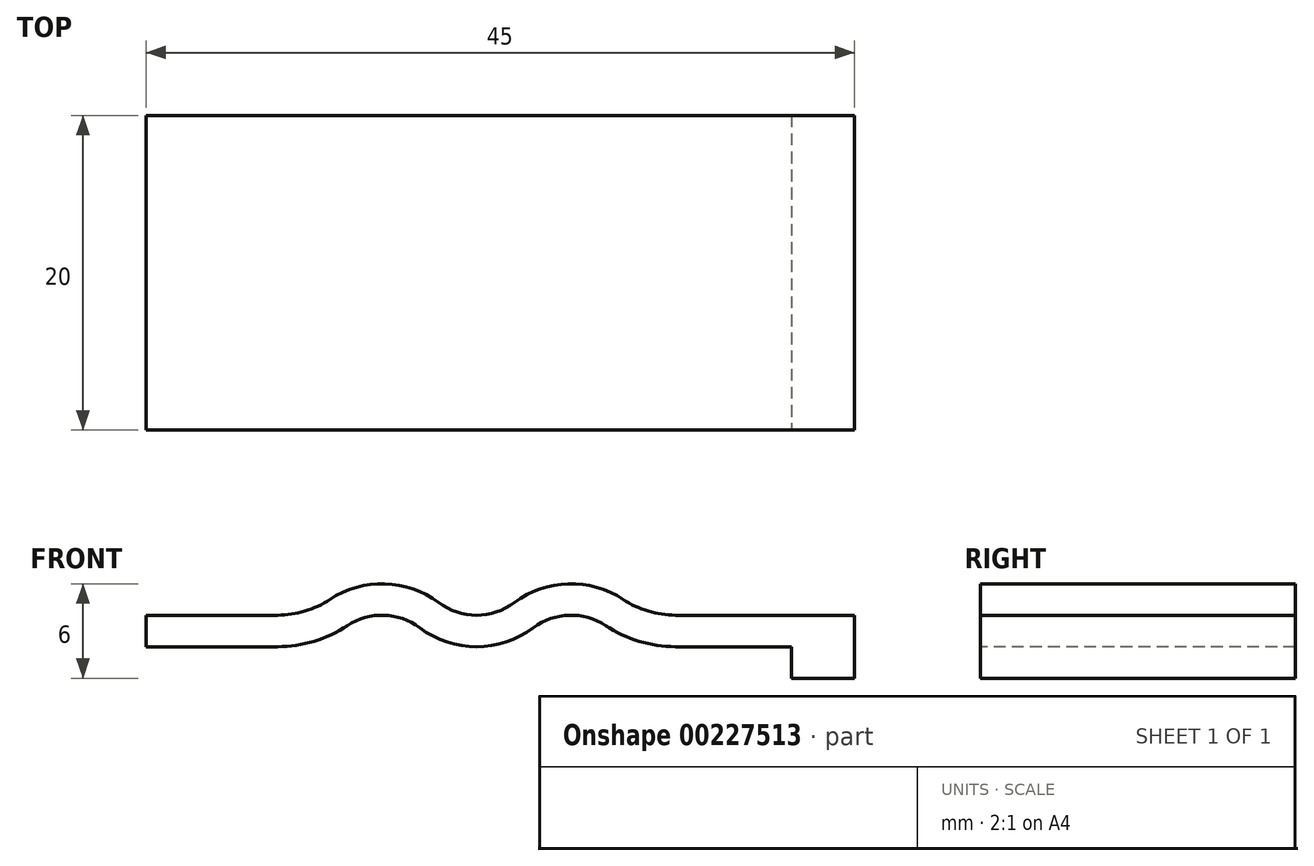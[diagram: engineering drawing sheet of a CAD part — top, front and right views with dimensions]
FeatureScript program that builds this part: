
annotation { "Feature Type Name" : "Feature", "Feature Type Description" : "" }
export const myFeature = defineFeature(function(context is Context, id is Id, definition is map)
    precondition{}
    {
        {
            var Q0;
            Q0=qCreatedBy(makeId("Front.planeOp"),FACE);
            var sketch = newSketch(context, id + "F0", { "sketchPlane" : qUnion([Q0])});
            skArc(sketch, "E0", {"start": v(-26.4, 4.8) * mm, "mid": v(-29.83, 6) * mm, "end": v(-33.32, 5) * mm});
            skArc(sketch, "E1", {"start": v(-26.4, 4.8) * mm, "mid": v(-24, 4) * mm, "end": v(-21.6, 4.8) * mm});
            skArc(sketch, "E2", {"start": v(-14.68, 5) * mm, "mid": v(-18.17, 6) * mm, "end": v(-21.6, 4.8) * mm});
            skLineSegment(sketch, "E3", {"start": v(-45, 4) * mm, "end": v(-36.63, 4) * mm});
            skLineSegment(sketch, "E4.trimOffspring", {"start": v(-11.37, 4) * mm, "end": v(0, 4) * mm});
            skPoint(sketch, "E5.visualSharp", {"position": v(-34.47, 4) * mm});
            skArc(sketch, "E5.filletArc", {"start": v(-36.63, 4) * mm, "mid": v(-34.9, 4.26) * mm, "end": v(-33.32, 5) * mm});
            skPoint(sketch, "E6.visualSharp", {"position": v(-13.53, 4) * mm});
            skArc(sketch, "E6.filletArc", {"start": v(-14.68, 5) * mm, "mid": v(-13.1, 4.26) * mm, "end": v(-11.37, 4) * mm});
            skLineSegment(sketch, "E7.0", {"start": v(-11.37, 2) * mm, "end": v(-4, 2) * mm});
            skArc(sketch, "E7.1", {"start": v(-15.79, 3.33) * mm, "mid": v(-13.68, 2.34) * mm, "end": v(-11.37, 2) * mm});
            skArc(sketch, "E7.2", {"start": v(-15.79, 3.33) * mm, "mid": v(-18.12, 4) * mm, "end": v(-20.4, 3.2) * mm});
            skLineSegment(sketch, "E7.3", {"start": v(-45, 2) * mm, "end": v(-36.63, 2) * mm});
            skArc(sketch, "E7.4", {"start": v(-36.63, 2) * mm, "mid": v(-34.32, 2.34) * mm, "end": v(-32.21, 3.33) * mm});
            skArc(sketch, "E7.5", {"start": v(-27.6, 3.2) * mm, "mid": v(-29.88, 4) * mm, "end": v(-32.21, 3.33) * mm});
            skArc(sketch, "E7.6", {"start": v(-27.6, 3.2) * mm, "mid": v(-24, 2) * mm, "end": v(-20.4, 3.2) * mm});
            skLineSegment(sketch, "E8", {"start": v(0, 4) * mm, "end": v(0, 0) * mm});
            skLineSegment(sketch, "E9", {"start": v(0, 0) * mm, "end": v(-4, 0) * mm});
            skLineSegment(sketch, "E10", {"start": v(-4, 0) * mm, "end": v(-4, 2) * mm});
            skPoint(sketch, "E11.orphan", {"position": v(-4, 4) * mm});
            skLineSegment(sketch, "E12", {"start": v(-45, 4) * mm, "end": v(-45, 2) * mm});
            skSolve(sketch);
        }
        {
            var Q0;
            Q0=makeQuery(id+"F0.imprint","IMPRINT",FACE,{"disambiguationData":[TD([[makeQuery(id+"F0.imprint","IMPRINT",EDGE,{"derivedFrom":sQuery(id+"F0.wireOp",EDGE,"E0")}),1.0]])]});
            extrude(context, id + "F1", {"entities" : qUnion([Q0]), "oppositeDirection" : true, "depth" : 20 * mm});
        }
    });
